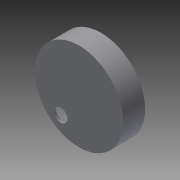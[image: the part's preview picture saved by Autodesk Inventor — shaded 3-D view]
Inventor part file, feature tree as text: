
AUTODESK INVENTOR PART (.ipt)
format: ipt  version: 2014 (Build 180170000, 170)  size: 173,056 bytes
history: native  units: mm
features: extrude x6, sketch x6, chamfer x3, projected_geometry x3
ambient origin geometry x8: Origin, YZ Plane, XZ Plane, XY Plane, X Axis, Y Axis, Z Axis, Center Point
bodies: Solid1 (feature_tree)
feature tree (18):
  extrude  "Extrusion1"  Depth=3.0mm TaperAngle=0.0deg
  extrude  "Extrusion2"  Depth=14.0mm TaperAngle=0.0deg
  extrude  "Extrusion3"  Depth=2.4mm
  chamfer  "Chamfer1"  Distance=14.0mm
  extrude  "Extrusion4"  Depth=2.0mm TaperAngle=45.0deg
  chamfer  "Chamfer2"  Distance=10.0mm
  extrude  "Extrusion5"  Depth=14.0mm TaperAngle=0.0deg
  extrude  "Extrusion6"  Depth=2.0mm TaperAngle=45.0deg
  chamfer  "Chamfer3"  Distance=20.0mm
  sketch  "Sketch1"  dims[d0=68.0mm d1=3.0mm d2=0.0mm]
  sketch  "Sketch2"  dims[d3=62.0mm d4=14.0mm d5=0.0mm]
  sketch  "Sketch3"  dims[d6=39.0mm d7=2.4mm]
  sketch  "Sketch4"  dims[d8=5.0mm]
  sketch  "Sketch5"  dims[d9=2.4mm]
  sketch  "Sketch6"  dims[d10=5.0mm d11=14.0mm d12=0.0mm d13=2.0mm d14=2.0mm d15=45.0deg d16=10.0mm d17=14.0mm d18=0.0mm d19=2.0mm d20=2.0mm d21=45.0deg d22=20.0mm d23=40.0mm d24=2.5mm d25=6.0mm d26=2.5mm d27=6.0mm d28=2.5mm d29=6.0mm d30=2.5mm d31=6.0mm d32=3.0mm d33=3.0mm d34=3.0mm d35=3.0mm d36=3.0mm d37=3.0mm d38=3.0mm d39=3.0mm d40=2.0mm d41=0.0mm d42=2.0mm d43=0.0mm d44=0.5mm d45=2.0mm d46=45.0deg]
  projected_geometry  "Projected Loop1"
  projected_geometry  "Projected Loop2"
  projected_geometry  "Projected Loop3"
